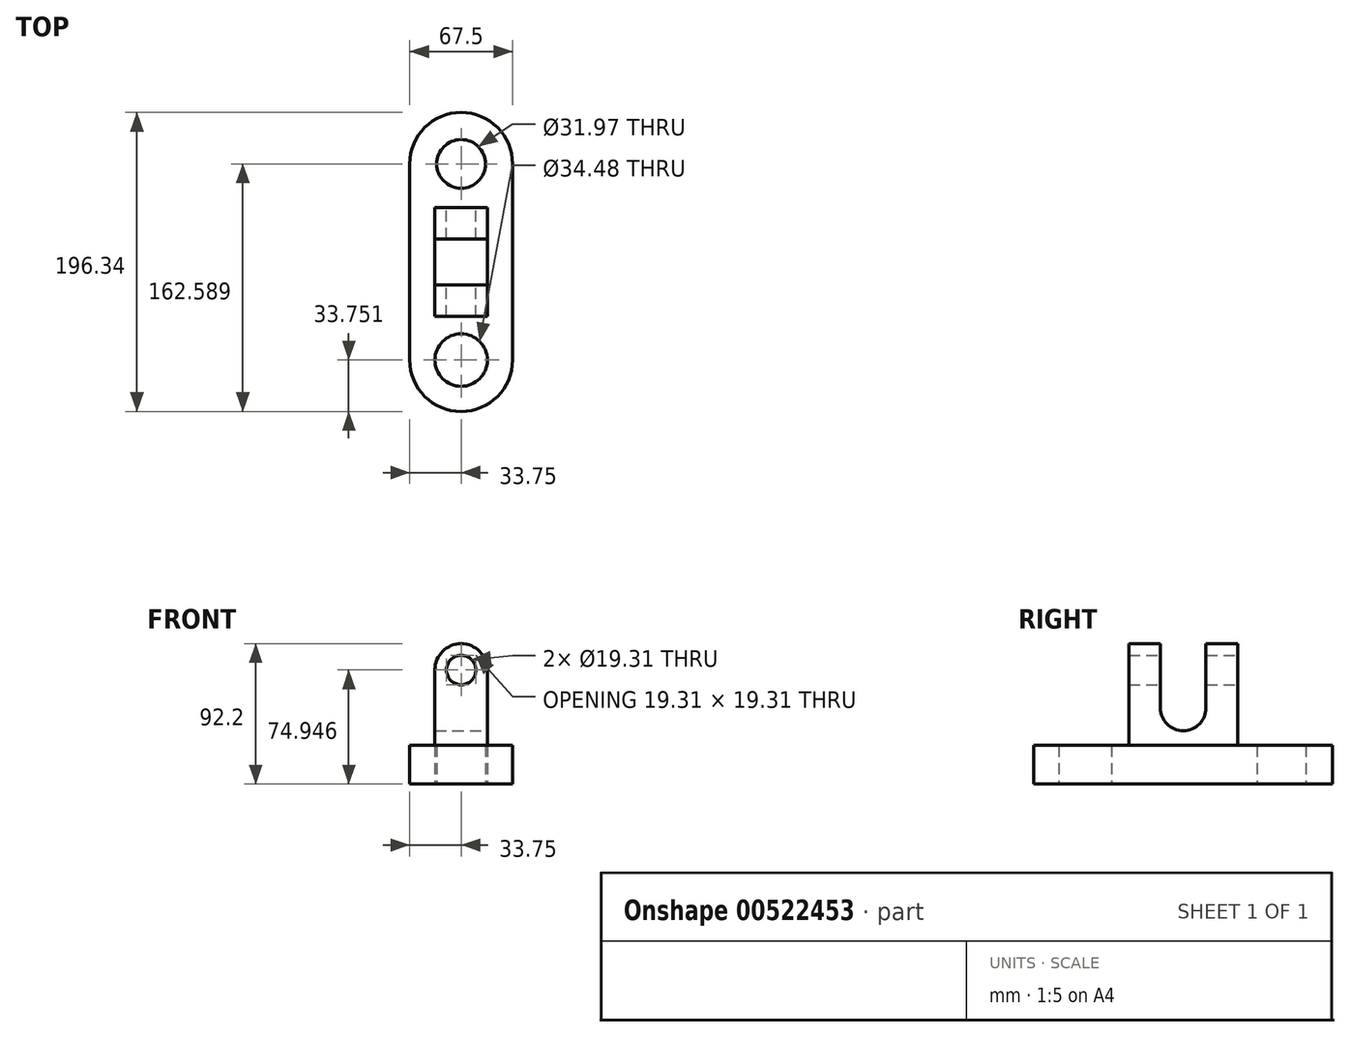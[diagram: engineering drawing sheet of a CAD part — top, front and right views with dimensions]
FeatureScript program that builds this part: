
annotation { "Feature Type Name" : "Feature", "Feature Type Description" : "" }
export const myFeature = defineFeature(function(context is Context, id is Id, definition is map)
    precondition{}
    {
        {
            var Q0;
            Q0=qCreatedBy(makeId("Top.planeOp"),FACE);
            var sketch = newSketch(context, id + "F0", { "sketchPlane" : qUnion([Q0])});
            skLineSegment(sketch, "E0.left", {"start": v(33.75, -64.42) * mm, "end": v(33.75, 64.42) * mm});
            skLineSegment(sketch, "E0.right", {"start": v(-33.75, -64.42) * mm, "end": v(-33.75, 64.42) * mm});
            skPoint(sketch, "E0.middle", {"position": v(0, 0) * mm});
            skArc(sketch, "E1", {"start": v(33.75, 64.42) * mm, "mid": v(0, 98.17) * mm, "end": v(-33.75, 64.42) * mm});
            skArc(sketch, "E2", {"start": v(33.75, -64.42) * mm, "mid": v(0, -98.17) * mm, "end": v(-33.75, -64.42) * mm});
            skCircle(sketch, "E3", {"center": v(0, 64.42) * mm, "radius": 15.99 * mm});
            skCircle(sketch, "E4", {"center": v(0, -64.42) * mm, "radius": 17.24 * mm});
            skSolve(sketch);
        }
        {
            var Q0;
            Q0 = qSketchRegion(id + "F0", true);
            extrude(context, id + "F1", {"entities" : qUnion([Q0]), "depth" : 25.4 * mm, "offsetDistance" : 25.4 * mm});
        }
        {
            var Q0;
            Q0=qCreatedBy(makeId("Front.planeOp"),FACE);
            var sketch = newSketch(context, id + "F2", { "sketchPlane" : qUnion([Q0])});
            skLineSegment(sketch, "E5.bottom", {"start": v(17.25, 24.34) * mm, "end": v(-17.25, 24.34) * mm});
            skLineSegment(sketch, "E5.left", {"start": v(17.25, 24.34) * mm, "end": v(17.25, 74.95) * mm});
            skLineSegment(sketch, "E5.right", {"start": v(-17.25, 24.34) * mm, "end": v(-17.25, 74.95) * mm});
            skPoint(sketch, "E5.middle", {"position": v(0, 49.64) * mm});
            skArc(sketch, "E6", {"start": v(17.25, 74.95) * mm, "mid": v(0, 92.2) * mm, "end": v(-17.25, 74.95) * mm});
            skCircle(sketch, "E7", {"center": v(0, 74.95) * mm, "radius": 9.65 * mm});
            skSolve(sketch);
        }
        {
            var Q0;
            Q0 = qSketchRegion(id + "F2", true);
            extrude(context, id + "F3", {"entities" : qUnion([Q0]), "operationType" : NewBodyOperationType.ADD, "endBound" : BoundingType.SYMMETRIC, "depth" : 71.63 * mm, "offsetDistance" : 25.4 * mm});
        }
        {
            var Q0;
            Q0=qCreatedBy(makeId("Right.planeOp"),FACE);
            var sketch = newSketch(context, id + "F4", { "sketchPlane" : qUnion([Q0])});
            skLineSegment(sketch, "E8.bottom", {"start": v(14.95, 50.03) * mm, "end": v(-14.95, 50.03) * mm});
            skLineSegment(sketch, "E8.top", {"start": v(14.95, 93.73) * mm, "end": v(-14.95, 93.73) * mm});
            skLineSegment(sketch, "E8.left", {"start": v(14.95, 50.03) * mm, "end": v(14.95, 93.73) * mm});
            skLineSegment(sketch, "E8.right", {"start": v(-14.95, 50.03) * mm, "end": v(-14.95, 93.73) * mm});
            skPoint(sketch, "E8.middle", {"position": v(0, 71.88) * mm});
            skCircle(sketch, "E9", {"center": v(0, 50.03) * mm, "radius": 14.95 * mm});
            skSolve(sketch);
        }
        {
            var Q0;
            Q0 = qSketchRegion(id + "F4", true);
            extrude(context, id + "F5", {"entities" : qUnion([Q0]), "operationType" : NewBodyOperationType.REMOVE, "endBound" : BoundingType.SYMMETRIC, "oppositeDirection" : true, "depth" : 1270 * mm, "offsetDistance" : 25.4 * mm});
        }
    });
